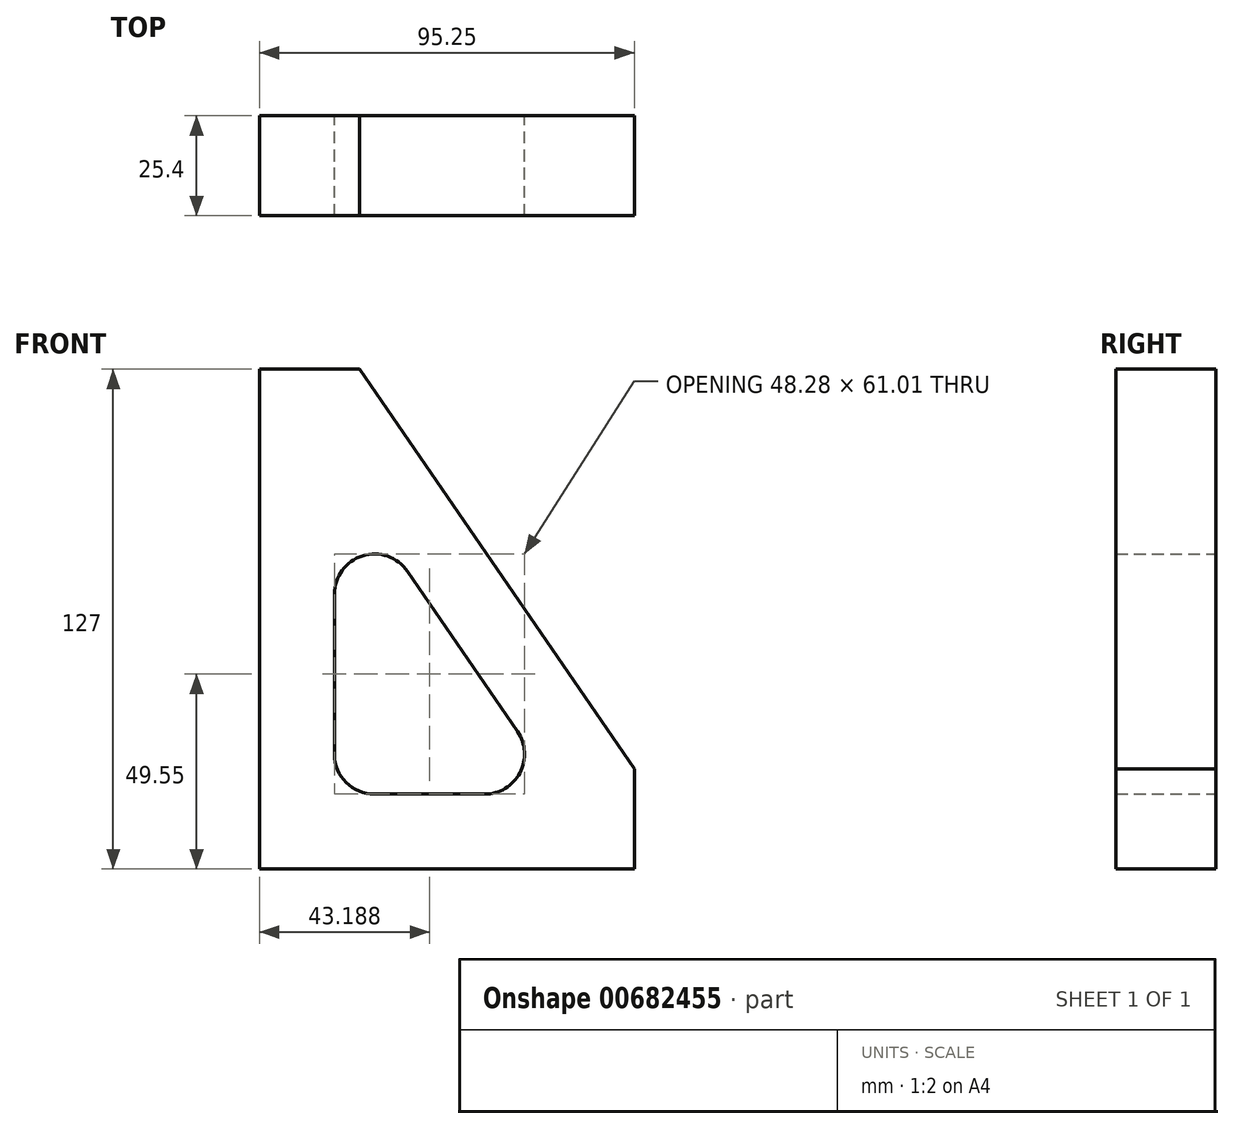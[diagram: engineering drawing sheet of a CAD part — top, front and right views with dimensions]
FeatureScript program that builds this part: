
annotation { "Feature Type Name" : "Feature", "Feature Type Description" : "" }
export const myFeature = defineFeature(function(context is Context, id is Id, definition is map)
    precondition{}
    {
        {
            var Q0;
            Q0=makeQuery(id+"FrR2ElmvHaNnCxS_0.imprint","IMPRINT",FACE,{"disambiguationData":[TD([[makeQuery(id+"FrR2ElmvHaNnCxS_0.imprint","IMPRINT",EDGE,{"derivedFrom":sQuery(id+"FrR2ElmvHaNnCxS_0.wireOp",EDGE,"kGrWKIyB-UIPv-N62U-JpKb-cba5M56u9zEY")}),-1.0]])]});
            var sketch = newSketch(context, id + "F0", { "sketchPlane" : qUnion([Q0])});
            skSolve(sketch);
        }
        {
            var Q0;
            Q0=makeQuery(id+"FrR2ElmvHaNnCxS_0.imprint","IMPRINT",FACE,{"disambiguationData":[TD([[makeQuery(id+"FrR2ElmvHaNnCxS_0.imprint","IMPRINT",EDGE,{"derivedFrom":sQuery(id+"FrR2ElmvHaNnCxS_0.wireOp",EDGE,"kGrWKIyB-UIPv-N62U-JpKb-cba5M56u9zEY")}),-1.0]])]});
            var sketch = newSketch(context, id + "F1", { "sketchPlane" : qUnion([Q0])});
            skLineSegment(sketch, "E0.0", {"start": v(11.03, -49.2) * mm, "end": v(-58.76, 52.12) * mm});
            skLineSegment(sketch, "E1.0", {"start": v(33.07, -36.42) * mm, "end": v(-39.73, 69.28) * mm});
            skLineSegment(sketch, "E1.1", {"start": v(33.07, -70.45) * mm, "end": v(33.07, -36.42) * mm});
            skLineSegment(sketch, "E1.2", {"start": v(-39.73, 69.28) * mm, "end": v(-74.83, 69.28) * mm});
            skLineSegment(sketch, "E1.3", {"start": v(-74.83, 69.28) * mm, "end": v(-74.83, -70.45) * mm});
            skLineSegment(sketch, "E1.4", {"start": v(-74.83, -70.45) * mm, "end": v(33.07, -70.45) * mm});
            skLineSegment(sketch, "E2.0", {"start": v(-68.48, -45.05) * mm, "end": v(26.72, -45.05) * mm});
            skLineSegment(sketch, "E3.0", {"start": v(-49.43, -64.1) * mm, "end": v(-49.43, 62.93) * mm});
            skSolve(sketch);
        }
        {
            var Q0;
            {var subQ0=makeQuery(id+"FrR2ElmvHaNnCxS_0.imprint","IMPRINT",EDGE,{"derivedFrom":sQuery(id+"FrR2ElmvHaNnCxS_0.wireOp",EDGE,"MuyBJmME-vZsc-EqDL-2OTa-f6YgZ13JuWDx")});Q0=makeQuery(id+"F1.imprint","IMPRINT",FACE,{"disambiguationData":[TD([[makeQuery(id+"F1.imprint","IMPRINT",EDGE,{"derivedFrom":subQ0}),1.0]])]});}
            var sketch = newSketch(context, id + "F2", { "sketchPlane" : qUnion([Q0])});
            skSolve(sketch);
        }
        {
            var Q0;
            Q0=qCreatedBy(makeId("Front.planeOp"),FACE);
            var sketch = newSketch(context, id + "F3", { "sketchPlane" : qUnion([Q0])});
            skLineSegment(sketch, "E4", {"start": v(-25.4, 61.36) * mm, "end": v(-25.4, -65.64) * mm});
            skLineSegment(sketch, "E5", {"start": v(-25.4, -65.64) * mm, "end": v(69.85, -65.64) * mm});
            skLineSegment(sketch, "E6", {"start": v(69.85, -65.64) * mm, "end": v(69.85, -40.24) * mm});
            skLineSegment(sketch, "E7", {"start": v(-25.4, 61.36) * mm, "end": v(0, 61.36) * mm});
            skLineSegment(sketch, "E8", {"start": v(0, 61.36) * mm, "end": v(69.85, -40.24) * mm});
            skLineSegment(sketch, "E9.0", {"start": v(12.18, 10.01) * mm, "end": v(40.16, -30.68) * mm});
            skLineSegment(sketch, "E10.0", {"start": v(-6.35, 4.26) * mm, "end": v(-6.35, -36.43) * mm});
            skLineSegment(sketch, "E11.0", {"start": v(3.81, -46.6) * mm, "end": v(31.78, -46.6) * mm});
            skArc(sketch, "E12.filletArc", {"start": v(12.18, 10.01) * mm, "mid": v(0.8, 13.96) * mm, "end": v(-6.35, 4.26) * mm});
            skArc(sketch, "E13.filletArc", {"start": v(31.78, -46.6) * mm, "mid": v(40.78, -41.16) * mm, "end": v(40.16, -30.68) * mm});
            skArc(sketch, "E14.filletArc", {"start": v(-6.35, -36.43) * mm, "mid": v(-3.37, -43.62) * mm, "end": v(3.81, -46.6) * mm});
            skSolve(sketch);
        }
        {
            var Q0;
            Q0 = qSketchRegion(id + "F3", true);
            extrude(context, id + "F4", {"entities" : qUnion([Q0]), "depth" : 25.4 * mm, "offsetDistance" : 25.4 * mm});
        }
    });
